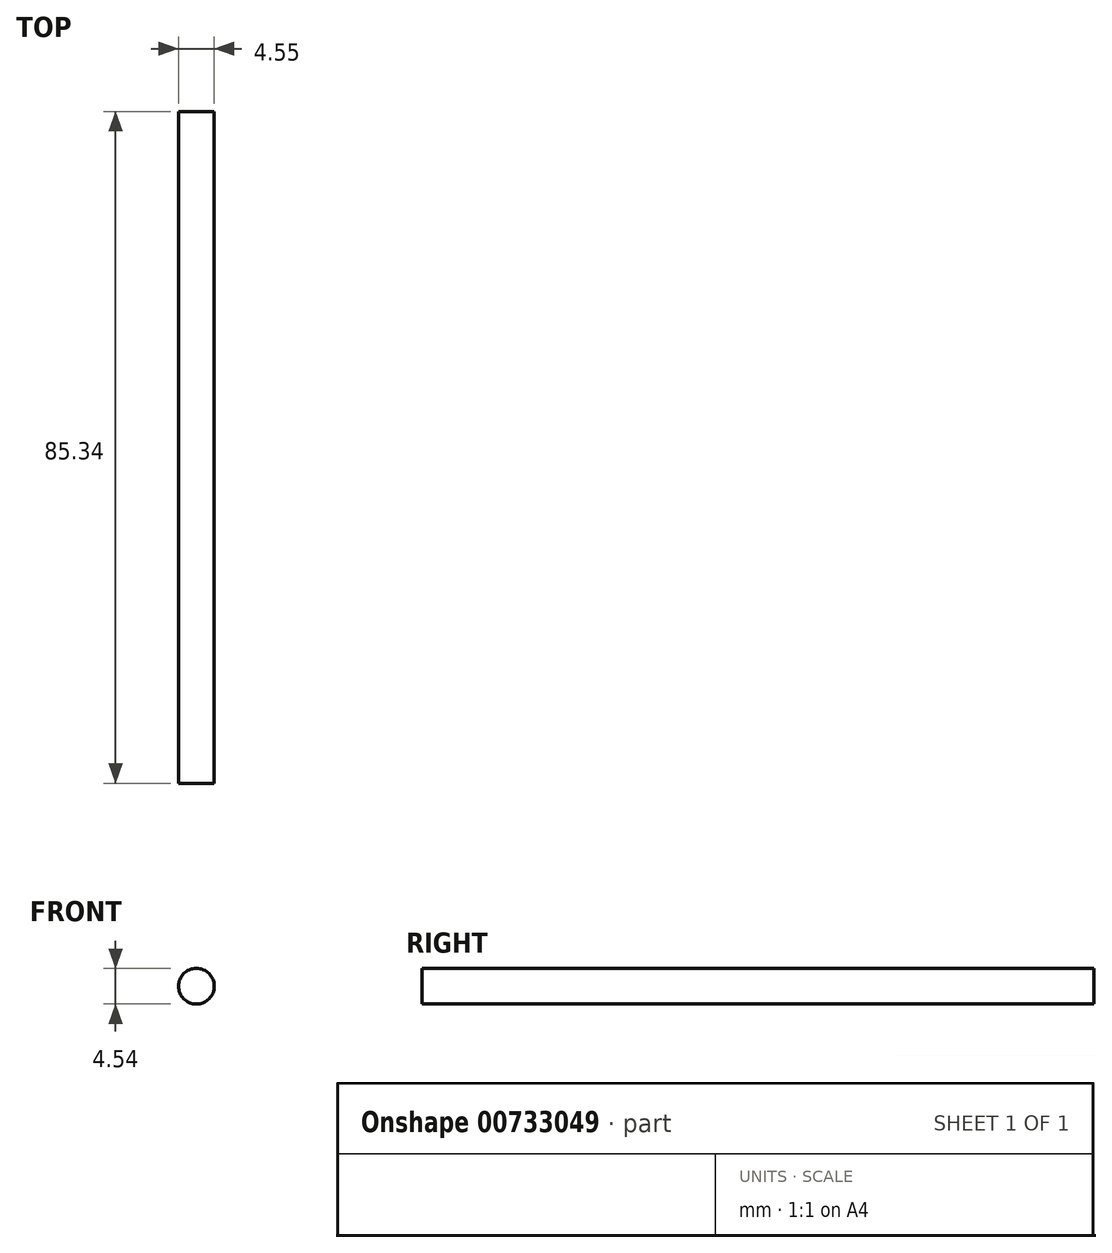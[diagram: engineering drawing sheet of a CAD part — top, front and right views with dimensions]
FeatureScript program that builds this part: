
annotation { "Feature Type Name" : "Feature", "Feature Type Description" : "" }
export const myFeature = defineFeature(function(context is Context, id is Id, definition is map)
    precondition{}
    {
        {
            var Q0;
            Q0=qCreatedBy(makeId("Front.planeOp"),FACE);
            var sketch = newSketch(context, id + "F0", { "sketchPlane" : qUnion([Q0])});
            skCircle(sketch, "E0", {"center": v(-51.44, 8.76) * mm, "radius": 2.27 * mm});
            skSolve(sketch);
        }
        {
            var Q0;
            Q0 = qSketchRegion(id + "F0", true);
            extrude(context, id + "F1", {"entities" : qUnion([Q0]), "depth" : 85.34 * mm, "offsetDistance" : 25.4 * mm});
        }
    });
